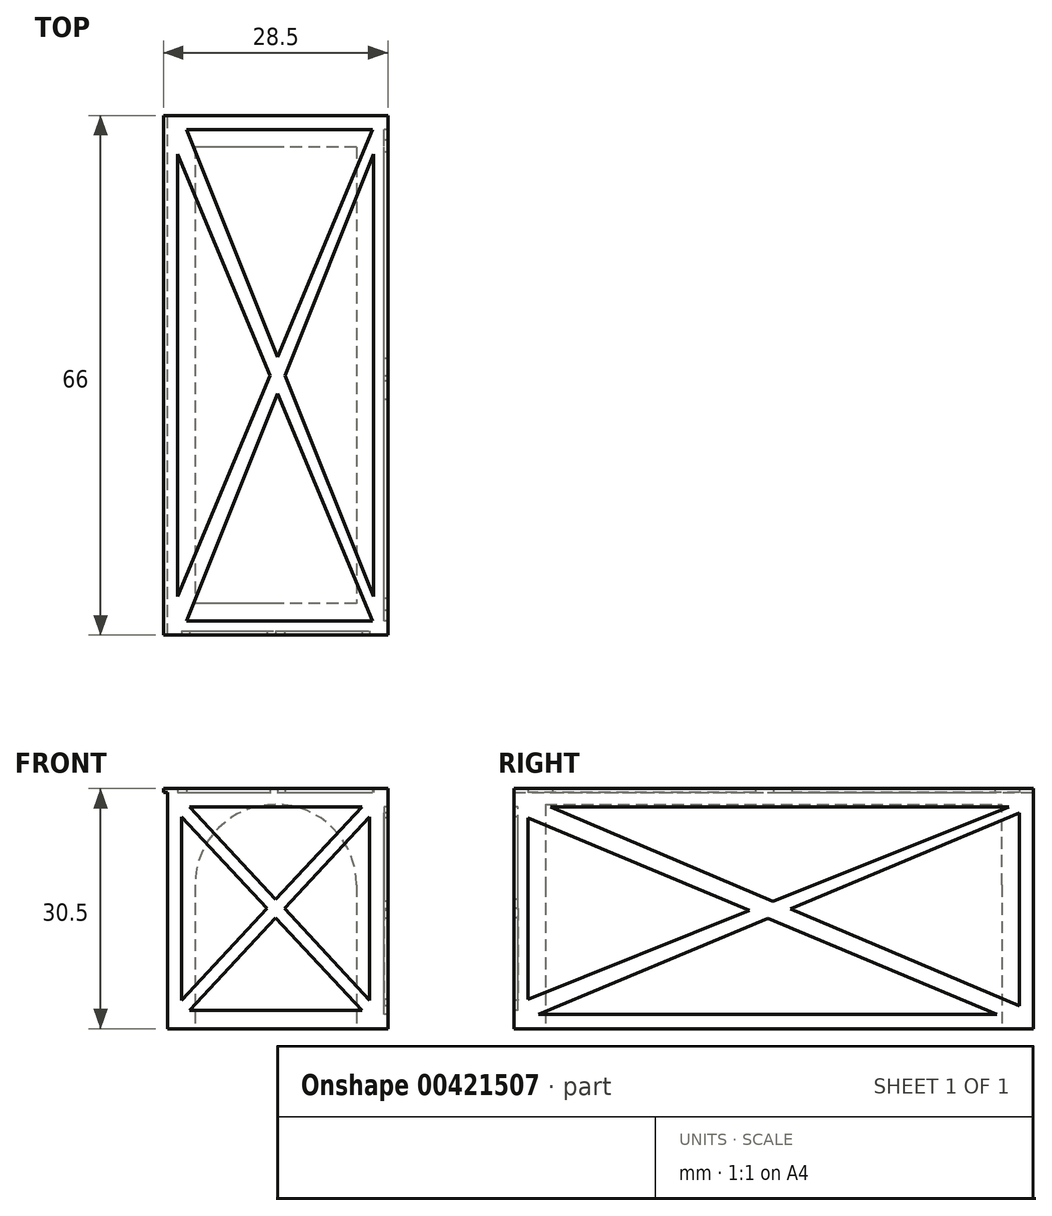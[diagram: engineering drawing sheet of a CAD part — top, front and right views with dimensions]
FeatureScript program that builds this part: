
annotation { "Feature Type Name" : "Feature", "Feature Type Description" : "" }
export const myFeature = defineFeature(function(context is Context, id is Id, definition is map)
    precondition{}
    {
        {
            var Q0;
            Q0=qCreatedBy(makeId("Top.planeOp"),FACE);
            var sketch = newSketch(context, id + "F0", { "sketchPlane" : qUnion([Q0])});
            skLineSegment(sketch, "E0.bottom", {"start": v(13.75, -33) * mm, "end": v(-13.75, -33) * mm});
            skLineSegment(sketch, "E0.top", {"start": v(13.75, 33) * mm, "end": v(-13.75, 33) * mm});
            skLineSegment(sketch, "E0.left", {"start": v(13.75, -33) * mm, "end": v(13.75, 33) * mm});
            skLineSegment(sketch, "E0.right", {"start": v(-13.75, -33) * mm, "end": v(-13.75, 33) * mm});
            skPoint(sketch, "E0.middle", {"position": v(0, 0) * mm});
            skSolve(sketch);
        }
        {
            var Q0;
            Q0=qSketchRegion(id+"F0",true);
            extrude(context, id + "F1", {"entities" : qUnion([Q0]), "depth" : 30 * mm});
        }
        {
            var Q0;
            Q0=makeQuery(id+"F1.opExtrude","SWEPT_FACE",FACE,{"disambiguationData":[OSD([sQuery(id+"F0.wireOp",EDGE,"E0.left")])]});
            var sketch = newSketch(context, id + "F2", { "sketchPlane" : qUnion([Q0])});
            skLineSegment(sketch, "E1", {"start": v(-33, 30) * mm, "end": v(-33, 0) * mm});
            skLineSegment(sketch, "E2", {"start": v(-33, 0) * mm, "end": v(33, 0) * mm});
            skLineSegment(sketch, "E3", {"start": v(33, 0) * mm, "end": v(33, 30) * mm});
            skLineSegment(sketch, "E4", {"start": v(33, 30) * mm, "end": v(-33, 30) * mm});
            skLineSegment(sketch, "E5", {"start": v(-31.2, 26.8) * mm, "end": v(-31.2, 3.73) * mm});
            skLineSegment(sketch, "E6", {"start": v(-29.87, 1.8) * mm, "end": v(28.37, 1.8) * mm});
            skLineSegment(sketch, "E7", {"start": v(31.2, 2.92) * mm, "end": v(31.2, 27.43) * mm});
            skLineSegment(sketch, "E8", {"start": v(-28.37, 28.2) * mm, "end": v(29.87, 28.2) * mm});
            skLineSegment(sketch, "E9.0", {"start": v(-31.2, 26.8) * mm, "end": v(-3.08, 15) * mm});
            skLineSegment(sketch, "E10.0", {"start": v(-28.37, 28.2) * mm, "end": v(-0.1, 16.2) * mm});
            skLineSegment(sketch, "E11.0", {"start": v(-29.87, 1.8) * mm, "end": v(-0.75, 14.02) * mm});
            skLineSegment(sketch, "E12.0", {"start": v(-31.2, 3.73) * mm, "end": v(-3.08, 15) * mm});
            skLineSegment(sketch, "E13.trimOffspring", {"start": v(-0.1, 16.2) * mm, "end": v(29.87, 28.2) * mm});
            skLineSegment(sketch, "E14.trimOffspring", {"start": v(2.15, 15.24) * mm, "end": v(31.2, 2.92) * mm});
            skLineSegment(sketch, "E15.trimOffspring", {"start": v(2.15, 15.24) * mm, "end": v(31.2, 27.43) * mm});
            skLineSegment(sketch, "E16.trimOffspring", {"start": v(-0.75, 14.02) * mm, "end": v(28.37, 1.8) * mm});
            skSolve(sketch);
        }
        {
            var Q0;
            Q0=qSketchRegion(id+"F2",true);
            extrude(context, id + "F3", {"entities" : qUnion([Q0]), "operationType" : NewBodyOperationType.ADD, "depth" : 0.5 * mm});
        }
        {
            var Q0;
            {var subQ0=sQuery(id+"F2.wireOp",EDGE,"E4");Q0=makeQuery(id+"Fi2ehXyChXqGkiH_1.1.F3.boolean.opBoolean","MERGE",FACE,{"derivedFrom":[makeQuery(id+"F3.boolean.opBoolean","MERGE",FACE,{"derivedFrom":[makeQuery(id+"F1.opExtrude","CAP_FACE",FACE,{"disambiguationData":[OSD([sQuery(id+"F0.wireOp",EDGE,"E0.bottom"),sQuery(id+"F0.wireOp",EDGE,"E0.top"),sQuery(id+"F0.wireOp",EDGE,"E0.left"),sQuery(id+"F0.wireOp",EDGE,"E0.right")])],"isStart":false}),makeQuery(id+"F3.opExtrude","SWEPT_FACE",FACE,{"disambiguationData":[OSD([subQ0])]})]}),makeQuery(id+"Fi2ehXyChXqGkiH_1.1.F3.opExtrude","SWEPT_FACE",FACE,{"disambiguationData":[OSD([subQ0])]})]});}
            var sketch = newSketch(context, id + "F4", { "sketchPlane" : qUnion([Q0])});
            skLineSegment(sketch, "E17", {"start": v(-14.25, -33) * mm, "end": v(-14.25, 33) * mm});
            skLineSegment(sketch, "E18", {"start": v(-14.25, 33) * mm, "end": v(14.25, 33) * mm});
            skLineSegment(sketch, "E19", {"start": v(14.25, 33) * mm, "end": v(14.25, -33) * mm});
            skLineSegment(sketch, "E20", {"start": v(14.25, -33) * mm, "end": v(-14.25, -33) * mm});
            skLineSegment(sketch, "E21.0", {"start": v(12.29, -31.2) * mm, "end": v(-11.31, -31.2) * mm});
            skLineSegment(sketch, "E22.0", {"start": v(-11.31, 31.2) * mm, "end": v(12.29, 31.2) * mm});
            skLineSegment(sketch, "E23.0", {"start": v(-12.45, -28.11) * mm, "end": v(-12.45, 28.11) * mm});
            skLineSegment(sketch, "E24.0", {"start": v(12.45, 28.11) * mm, "end": v(12.45, -28.11) * mm});
            skLineSegment(sketch, "E25.0", {"start": v(-12.45, 28.11) * mm, "end": v(-0.73, 0) * mm});
            skLineSegment(sketch, "E26.0", {"start": v(-11.31, 31.2) * mm, "end": v(0.25, 2.34) * mm});
            skLineSegment(sketch, "E27.0", {"start": v(-11.31, -31.2) * mm, "end": v(0.25, -2.34) * mm});
            skLineSegment(sketch, "E28.0", {"start": v(-12.45, -28.11) * mm, "end": v(-0.73, 0) * mm});
            skLineSegment(sketch, "E29.trimOffspring", {"start": v(0.25, 2.34) * mm, "end": v(12.29, 31.2) * mm});
            skLineSegment(sketch, "E30.trimOffspring", {"start": v(1.19, 0) * mm, "end": v(12.45, -28.11) * mm});
            skLineSegment(sketch, "E31.trimOffspring", {"start": v(1.19, 0) * mm, "end": v(12.45, 28.11) * mm});
            skLineSegment(sketch, "E32.trimOffspring", {"start": v(0.25, -2.34) * mm, "end": v(12.29, -31.2) * mm});
            skSolve(sketch);
        }
        {
            var Q0;
            Q0=qSketchRegion(id+"F4",true);
            extrude(context, id + "F5", {"entities" : qUnion([Q0]), "operationType" : NewBodyOperationType.ADD, "depth" : 0.5 * mm});
        }
        {
            var Q0;
            {var subQ0=sQuery(id+"F2.wireOp",EDGE,"E1");Q0=makeQuery(id+"F5.boolean.opBoolean","MERGE",FACE,{"derivedFrom":[makeQuery(id+"Fi2ehXyChXqGkiH_1.1.F3.boolean.opBoolean","MERGE",FACE,{"derivedFrom":[makeQuery(id+"F3.boolean.opBoolean","MERGE",FACE,{"derivedFrom":[makeQuery(id+"F1.opExtrude","SWEPT_FACE",FACE,{"disambiguationData":[OSD([sQuery(id+"F0.wireOp",EDGE,"E0.bottom")])]}),makeQuery(id+"F3.opExtrude","SWEPT_FACE",FACE,{"disambiguationData":[OSD([subQ0])]})]}),makeQuery(id+"Fi2ehXyChXqGkiH_1.1.F3.opExtrude","SWEPT_FACE",FACE,{"disambiguationData":[OSD([subQ0])]})]}),makeQuery(id+"F5.opExtrude","SWEPT_FACE",FACE,{"disambiguationData":[OSD([sQuery(id+"F4.wireOp",EDGE,"E20")])]})]});}
            var sketch = newSketch(context, id + "F6", { "sketchPlane" : qUnion([Q0])});
            skLineSegment(sketch, "E33.0", {"start": v(-10.96, 2.3) * mm, "end": v(10.96, 2.3) * mm});
            skLineSegment(sketch, "E33.1", {"start": v(-11.95, 26.89) * mm, "end": v(-11.95, 3.61) * mm});
            skLineSegment(sketch, "E33.2", {"start": v(10.96, 28.2) * mm, "end": v(-10.96, 28.2) * mm});
            skLineSegment(sketch, "E33.3", {"start": v(11.95, 3.61) * mm, "end": v(11.95, 26.89) * mm});
            skLineSegment(sketch, "E34.0", {"start": v(-11.95, 26.89) * mm, "end": v(-1.1, 15.25) * mm});
            skLineSegment(sketch, "E35.0", {"start": v(-10.96, 28.2) * mm, "end": v(0, 16.44) * mm});
            skLineSegment(sketch, "E36.0", {"start": v(-10.96, 2.3) * mm, "end": v(0, 14.06) * mm});
            skLineSegment(sketch, "E37.0", {"start": v(-11.95, 3.61) * mm, "end": v(-1.1, 15.25) * mm});
            skLineSegment(sketch, "E38.trimOffspring", {"start": v(1.1, 15.25) * mm, "end": v(11.95, 3.61) * mm});
            skLineSegment(sketch, "E39.trimOffspring", {"start": v(0, 16.44) * mm, "end": v(10.96, 28.2) * mm});
            skLineSegment(sketch, "E40.trimOffspring", {"start": v(1.1, 15.25) * mm, "end": v(11.95, 26.89) * mm});
            skLineSegment(sketch, "E41.trimOffspring", {"start": v(0, 14.06) * mm, "end": v(10.96, 2.3) * mm});
            skSolve(sketch);
        }
        {
            var Q0;
            Q0=qSketchRegion(id+"F6",true);
            extrude(context, id + "F7", {"entities" : qUnion([Q0]), "operationType" : NewBodyOperationType.REMOVE, "oppositeDirection" : true, "depth" : 0.5 * mm});
        }
        {
            var Q0;
            {var subQ0=sQuery(id+"F2.wireOp",EDGE,"E2");Q0=makeQuery(id+"Fi2ehXyChXqGkiH_1.1.F3.boolean.opBoolean","MERGE",FACE,{"derivedFrom":[makeQuery(id+"F3.boolean.opBoolean","MERGE",FACE,{"derivedFrom":[makeQuery(id+"F1.opExtrude","CAP_FACE",FACE,{"disambiguationData":[OSD([sQuery(id+"F0.wireOp",EDGE,"E0.bottom"),sQuery(id+"F0.wireOp",EDGE,"E0.top"),sQuery(id+"F0.wireOp",EDGE,"E0.left"),sQuery(id+"F0.wireOp",EDGE,"E0.right")])],"isStart":true}),makeQuery(id+"F3.opExtrude","SWEPT_FACE",FACE,{"disambiguationData":[OSD([subQ0])]})]}),makeQuery(id+"Fi2ehXyChXqGkiH_1.1.F3.opExtrude","SWEPT_FACE",FACE,{"disambiguationData":[OSD([subQ0])]})]});}
            var sketch = newSketch(context, id + "F8", { "sketchPlane" : qUnion([Q0])});
            skLineSegment(sketch, "E42.bottom", {"start": v(10.25, -29) * mm, "end": v(-10.25, -29) * mm});
            skLineSegment(sketch, "E42.top", {"start": v(10.25, 29) * mm, "end": v(-10.25, 29) * mm});
            skLineSegment(sketch, "E42.left", {"start": v(10.25, -29) * mm, "end": v(10.25, 29) * mm});
            skLineSegment(sketch, "E42.right", {"start": v(-10.25, -29) * mm, "end": v(-10.25, 29) * mm});
            skPoint(sketch, "E42.middle", {"position": v(0, 0) * mm});
            skSolve(sketch);
        }
        {
            var Q0;
            Q0=qSketchRegion(id+"F8",true);
            extrude(context, id + "F9", {"entities" : qUnion([Q0]), "operationType" : NewBodyOperationType.REMOVE, "oppositeDirection" : true, "depth" : (30.5 - 2) * mm});
        }
        {
            var Q0;
            Q0=makeQuery(id+"F9.boolean.opBoolean","COPY",EDGE,{"derivedFrom":makeQuery(id+"F9.opExtrude","CAP_EDGE",EDGE,{"disambiguationData":[OSD([sQuery(id+"F8.wireOp",EDGE,"E42.right")])],"isStart":false})});
            fillet(context, id + "F10", {"entities" : qUnion([Q0]), "radius" : (20.5 / 2) * mm, "tangentPropagation" : true, "allowEdgeOverflow" : false});
        }
        {
            var Q0;
            Q0=makeQuery(id+"F9.boolean.opBoolean","COPY",EDGE,{"derivedFrom":makeQuery(id+"F9.opExtrude","CAP_EDGE",EDGE,{"disambiguationData":[OSD([sQuery(id+"F8.wireOp",EDGE,"E42.left")])],"isStart":false})});
            fillet(context, id + "F11", {"entities" : qUnion([Q0]), "radius" : (20.5 / 2) * mm, "tangentPropagation" : true, "allowEdgeOverflow" : false});
        }
    });
